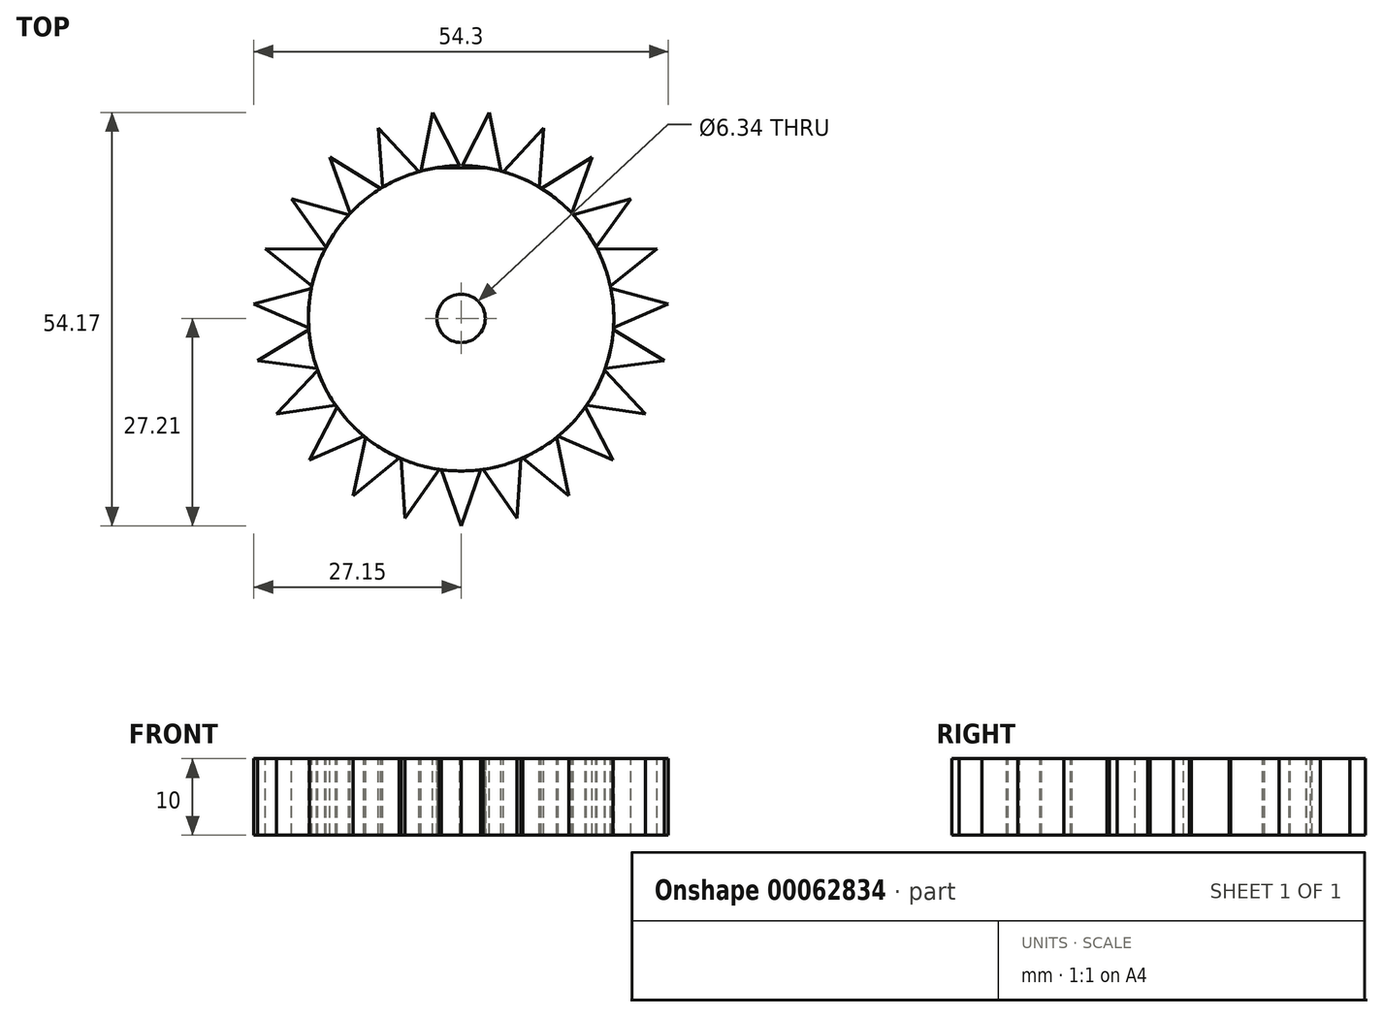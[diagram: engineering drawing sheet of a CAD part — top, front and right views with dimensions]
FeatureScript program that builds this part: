
annotation { "Feature Type Name" : "Feature", "Feature Type Description" : "" }
export const myFeature = defineFeature(function(context is Context, id is Id, definition is map)
    precondition{}
    {
        {
            var Q0;
            Q0=qCreatedBy(makeId("Top.planeOp"),FACE);
            var sketch = newSketch(context, id + "F0", { "sketchPlane" : qUnion([Q0])});
            skCircle(sketch, "E0", {"center": v(0, 0) * mm, "radius": 20 * mm});
            skLineSegment(sketch, "E1", {"start": v(0, 27.28) * mm, "end": v(-3.19, 19.74) * mm});
            skLineSegment(sketch, "E2", {"start": v(0, 27.28) * mm, "end": v(3.19, 19.74) * mm});
            skLineSegment(sketch, "E3", {"start": v(-3.19, 19.74) * mm, "end": v(3.19, 19.74) * mm});
            skSolve(sketch);
        }
        {
            var Q0;
            {var subQ0=sQuery(id+"F0.wireOp",EDGE,"E3");Q0=makeQuery(id+"F0.imprint","IMPRINT",FACE,{"disambiguationData":[TD([[makeQuery(id+"F0.imprint","IMPRINT",EDGE,{"derivedFrom":subQ0}),-1.0]])]});}
            extrude(context, id + "F1", {"entities" : qUnion([Q0]), "depth" : 10 * mm});
        }
        {
            var Q0;
            Q0=makeQuery(id+"F1.opExtrude","CAP_FACE",FACE,{"disambiguationData":[OSD([sQuery(id+"F0.wireOp",EDGE,"E0"),sQuery(id+"F0.wireOp",EDGE,"E3")])],"isStart":false});
            var sketch = newSketch(context, id + "F2", { "sketchPlane" : qUnion([Q0])});
            skLineSegment(sketch, "E4", {"start": v(-2.58, -19.83) * mm, "end": v(0, -27.2) * mm});
            skPoint(sketch, "E4.endSnap0", {"position": v(0, -20) * mm});
            skLineSegment(sketch, "E5", {"start": v(0, -27.2) * mm, "end": v(2.58, -19.83) * mm});
            skSolve(sketch);
        }
        {
            var Q0;
            {var subQ0=sQuery(id+"F2.wireOp",EDGE,"E4");Q0=makeQuery(id+"F2.imprint","IMPRINT",FACE,{"disambiguationData":[TD([[makeQuery(id+"F2.imprint","IMPRINT",EDGE,{"derivedFrom":subQ0}),1.0]])]});}
            extrude(context, id + "F3", {"entities" : qUnion([Q0]), "oppositeDirection" : true, "depth" : 10 * mm});
        }
        {
            var Q0;
            Q0=makeQuery(id+"F3.opExtrude","SWEPT_BODY",BODY,{"disambiguationData":[OSD([sQuery(id+"F0.wireOp",EDGE,"E0"),sQuery(id+"F2.wireOp",EDGE,"E4"),sQuery(id+"F2.wireOp",EDGE,"E5")])]});
            var Q1;
            Q1=makeQuery(id+"F1.opExtrude","SWEPT_FACE",FACE,{"disambiguationData":[OSD([sQuery(id+"F0.wireOp",EDGE,"E0")])]});
            circularPattern(context, id + "F4", {"entities" : qUnion([Q0]), "axis" : qUnion([Q1]), "angle" : 360 * degree, "instanceCount" : 23, "equalSpace" : true});
        }
        {
            var Q0;
            Q0=makeQuery(id+"F1.opExtrude","CAP_FACE",FACE,{"disambiguationData":[OSD([sQuery(id+"F0.wireOp",EDGE,"E0"),sQuery(id+"F0.wireOp",EDGE,"E3")])],"isStart":false});
            var sketch = newSketch(context, id + "F5", { "sketchPlane" : qUnion([Q0])});
            skCircle(sketch, "E6", {"center": v(0, 0) * mm, "radius": 3.17 * mm});
            skSolve(sketch);
        }
        {
            var Q0;
            Q0=makeQuery(id+"F5.imprint","IMPRINT",FACE,{"disambiguationData":[TD([[makeQuery(id+"F5.imprint","IMPRINT",EDGE,{"derivedFrom":sQuery(id+"F5.wireOp",EDGE,"E6")}),1.0]])]});
            extrude(context, id + "F6", {"entities" : qUnion([Q0]), "operationType" : NewBodyOperationType.REMOVE, "oppositeDirection" : true, "depth" : 25 * mm});
        }
    });
